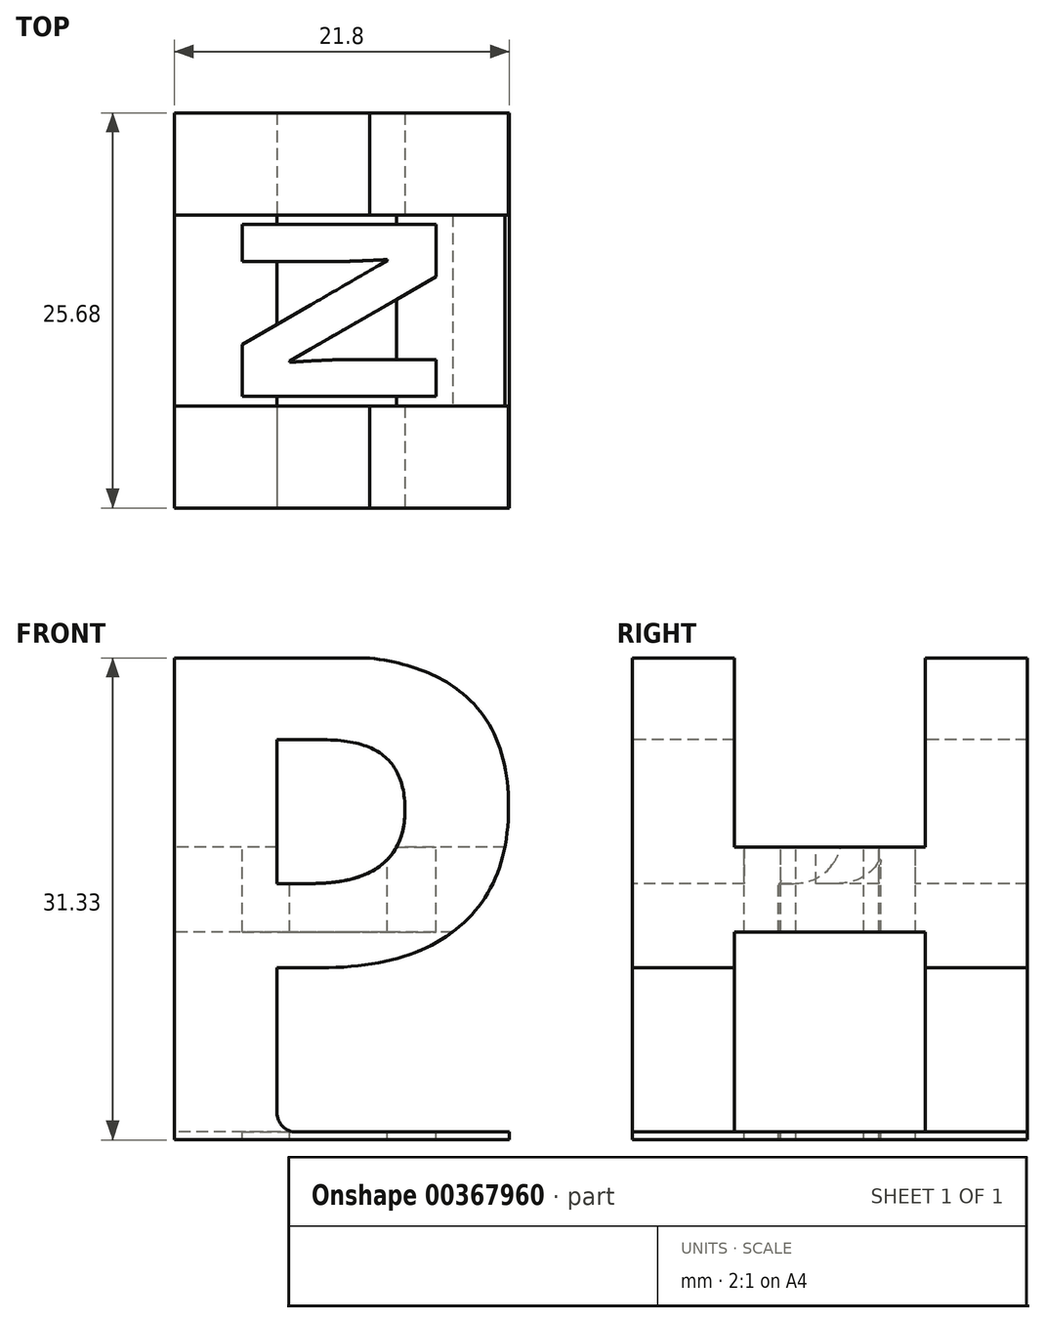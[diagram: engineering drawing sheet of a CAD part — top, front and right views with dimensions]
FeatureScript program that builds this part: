
annotation { "Feature Type Name" : "Feature", "Feature Type Description" : "" }
export const myFeature = defineFeature(function(context is Context, id is Id, definition is map)
    precondition{}
    {
        {
            var Q0;
            Q0=qCreatedBy(makeId("Front.planeOp"),FACE);
            var sketch = newSketch(context, id + "F0", { "sketchPlane" : qUnion([Q0])});
            skLineSegment(sketch, "E0.bottom", {"start": v(15.88, 15.88) * mm, "end": v(-15.88, 15.88) * mm});
            skLineSegment(sketch, "E0.top", {"start": v(15.88, -15.88) * mm, "end": v(-15.88, -15.88) * mm});
            skLineSegment(sketch, "E0.left", {"start": v(15.88, 15.88) * mm, "end": v(15.88, -15.88) * mm});
            skLineSegment(sketch, "E0.right", {"start": v(-15.88, 15.88) * mm, "end": v(-15.88, -15.88) * mm});
            skPoint(sketch, "E0.middle", {"position": v(0, 0) * mm});
            skSolve(sketch);
        }
        {
            var Q0;
            Q0=qSketchRegion(id+"F0",true);
            extrude(context, id + "F1", {"entities" : qUnion([Q0]), "depth" : 31.75 * mm});
        }
        {
            var Q0;
            Q0=makeQuery(id+"F1.opExtrude","CAP_FACE",FACE,{"disambiguationData":[OSD([sQuery(id+"F0.wireOp",EDGE,"E0.bottom"),sQuery(id+"F0.wireOp",EDGE,"E0.top"),sQuery(id+"F0.wireOp",EDGE,"E0.left"),sQuery(id+"F0.wireOp",EDGE,"E0.right")])],"isStart":false});
            var sketch = newSketch(context, id + "F2", { "sketchPlane" : qUnion([Q0])});
            skText(sketch, "E1", { "text": "P", "fontName": "OpenSans-Bold.ttf"});
            skLineSegment(sketch, "E2.bottom", {"start": v(11.48, -15.37) * mm, "end": v(-5.52, -15.37) * mm});
            skLineSegment(sketch, "E2.top", {"start": v(11.48, -15.88) * mm, "end": v(-5.52, -15.88) * mm});
            skLineSegment(sketch, "E2.left", {"start": v(11.48, -15.37) * mm, "end": v(11.48, -15.88) * mm});
            skLineSegment(sketch, "E2.right", {"start": v(-5.52, -15.37) * mm, "end": v(-5.52, -15.88) * mm});
            skLineSegment(sketch, "E3", {"start": v(11.48, 13.63) * mm, "end": v(11.48, -15.88) * mm, "construction": true});
            const initialGuessF2  = {"E1": [-0.01428, -0.01588, 1, 0, 0.03175]};
            skSetInitialGuess(sketch, initialGuessF2);
            skSolve(sketch);
        }
        {
            var Q0;
            Q0=makeQuery(id+"F2.imprint","IMPRINT",FACE,{"disambiguationData":[TD([[makeQuery(id+"F2.imprint","IMPRINT",EDGE,{"derivedFrom":sQuery(id+"F2.wireOp",EDGE,"E1.sketch_text.stroke-7")}),1.0]])]});
            var Q1;
            Q1=makeQuery(id+"F2.imprint","IMPRINT",FACE,{"disambiguationData":[TD([[makeQuery(id+"F2.imprint","IMPRINT",EDGE,{"derivedFrom":sQuery(id+"F2.wireOp",EDGE,"E1.sketch_text.stroke-0")}),1.0]])]});
            var Q2;
            {var subQ6=sQuery(id+"F2.wireOp",EDGE,"E1.sketch_text.stroke-9");Q2=makeQuery(id+"F2.imprint","IMPRINT",FACE,{"disambiguationData":[TD([[makeQuery(id+"F2.imprint","IMPRINT",EDGE,{"derivedFrom":subQ6}),1.0]])]});}
            var Q3;
            {var subQ1=sQuery(id+"F2.wireOp",EDGE,"86d704e9-ed5c-438c-a19e-a56261acf02c.sketch_text.stroke-1");Q3=makeQuery(id+"F2.imprint","IMPRINT",FACE,{"disambiguationData":[TD([[makeQuery(id+"F2.imprint","IMPRINT",EDGE,{"derivedFrom":subQ1}),1.0]])]});}
            var Q4;
            {var subQ0=sQuery(id+"F2.wireOp",EDGE,"3e470cdb-64af-4909-ac97-25825973aa04.sketch_text.stroke-1");Q4=makeQuery(id+"F2.imprint","IMPRINT",FACE,{"disambiguationData":[TD([[makeQuery(id+"F2.imprint","IMPRINT",EDGE,{"derivedFrom":subQ0}),1.0]])]});}
            var Q5;
            {var subQ1=makeQuery(id+"F1.opExtrude","CAP_EDGE",EDGE,{"disambiguationData":[OSD([sQuery(id+"F0.wireOp",EDGE,"E0.top")])],"isStart":false});var subQ3=makeQuery(id+"F1.opExtrude","CAP_EDGE",EDGE,{"disambiguationData":[OSD([sQuery(id+"F0.wireOp",EDGE,"E0.left")])],"isStart":false});var subQ5=makeQuery(id+"F2.imprint","INTERSECT",VERTEX,{"derivedFrom":[subQ1,subQ3]});Q5=makeQuery(id+"F2.imprint","IMPRINT",FACE,{"disambiguationData":[TD([[makeQuery(id+"F2.imprint","IMPRINT",EDGE,{"disambiguationData":[TD([[subQ5,1.0]])],"derivedFrom":subQ3}),-1.0]])]});}
            var Q6;
            {var subQ5=sQuery(id+"F2.wireOp",EDGE,"86d704e9-ed5c-438c-a19e-a56261acf02c.sketch_text.stroke-11");Q6=makeQuery(id+"F2.imprint","IMPRINT",FACE,{"disambiguationData":[TD([[makeQuery(id+"F2.imprint","IMPRINT",EDGE,{"derivedFrom":subQ5}),1.0]])]});}
            var Q7;
            {var subQ0=sQuery(id+"F2.wireOp",EDGE,"86d704e9-ed5c-438c-a19e-a56261acf02c.sketch_text.stroke-0");Q7=makeQuery(id+"F2.imprint","IMPRINT",FACE,{"disambiguationData":[TD([[makeQuery(id+"F2.imprint","IMPRINT",EDGE,{"derivedFrom":subQ0}),-1.0]])]});}
            extrude(context, id + "F3", {"entities" : qUnion([Q0, Q1, Q2, Q3, Q4, Q5, Q6, Q7]), "operationType" : NewBodyOperationType.REMOVE, "endBound" : BoundingType.THROUGH_ALL, "oppositeDirection" : true, "depth" : 25.4 * mm});
        }
        {
            var Q0;
            Q0=makeQuery(id+"F3.boolean.opBoolean","COPY",FACE,{"derivedFrom":makeQuery(id+"F3.opExtrude","SWEPT_FACE",FACE,{"disambiguationData":[OSD([sQuery(id+"F2.wireOp",EDGE,"E1.sketch_text.stroke-12")])]})});
            var sketch = newSketch(context, id + "F4", { "sketchPlane" : qUnion([Q0])});
            skText(sketch, "E4", { "text": "H", "fontName": "OpenSans-Bold.ttf"});
            skLineSegment(sketch, "E5.bottom", {"start": v(8.61, -15.88) * mm, "end": v(23.96, -15.88) * mm});
            skLineSegment(sketch, "E5.top", {"start": v(8.61, -15.37) * mm, "end": v(23.96, -15.37) * mm});
            skLineSegment(sketch, "E5.left", {"start": v(8.61, -15.88) * mm, "end": v(8.61, -15.37) * mm});
            skLineSegment(sketch, "E5.right", {"start": v(23.96, -15.88) * mm, "end": v(23.96, -15.37) * mm});
            const initialGuessF4  = {"E4": [-0.0011, -0.01588, 1, 0, 0.0316]};
            skSetInitialGuess(sketch, initialGuessF4);
            skSolve(sketch);
        }
        {
            var Q0;
            {var subQ5=sQuery(id+"F4.wireOp",EDGE,"E4.sketch_text.stroke-5");Q0=makeQuery(id+"F4.imprint","IMPRINT",FACE,{"disambiguationData":[TD([[makeQuery(id+"F4.imprint","IMPRINT",EDGE,{"derivedFrom":subQ5}),1.0]])]});}
            var Q1;
            {var subQ0=sQuery(id+"F4.wireOp",EDGE,"E4.sketch_text.stroke-2");Q1=makeQuery(id+"F4.imprint","IMPRINT",FACE,{"disambiguationData":[TD([[makeQuery(id+"F4.imprint","IMPRINT",EDGE,{"derivedFrom":subQ0}),1.0]])]});}
            extrude(context, id + "F5", {"entities" : qUnion([Q0, Q1]), "operationType" : NewBodyOperationType.REMOVE, "endBound" : BoundingType.THROUGH_ALL, "oppositeDirection" : true, "depth" : 25.4 * mm});
        }
        {
            var Q0;
            Q0=makeQuery(id+"F5.boolean.opBoolean","COPY",FACE,{"derivedFrom":makeQuery(id+"F5.opExtrude","SWEPT_FACE",FACE,{"disambiguationData":[OSD([sQuery(id+"F4.wireOp",EDGE,"E4.sketch_text.stroke-6")])]})});
            var sketch = newSketch(context, id + "F6", { "sketchPlane" : qUnion([Q0])});
            skText(sketch, "E6", { "text": "N", "fontName": "OpenSans-Bold.ttf"});
            const initialGuessF6  = {"E6": [0.0067, -0.02285, 0, 1, 0.0127]};
            skSetInitialGuess(sketch, initialGuessF6);
            skSolve(sketch);
        }
        {
            var Q0;
            Q0=makeQuery(id+"F6.imprint","IMPRINT",FACE,{"disambiguationData":[TD([[makeQuery(id+"F6.imprint","IMPRINT",EDGE,{"derivedFrom":sQuery(id+"F6.wireOp",EDGE,"E6.sketch_text.stroke-0")}),-1.0]])]});
            extrude(context, id + "F7", {"entities" : qUnion([Q0]), "operationType" : NewBodyOperationType.REMOVE, "endBound" : BoundingType.THROUGH_ALL, "oppositeDirection" : true, "depth" : 25.4 * mm});
        }
        {
            var Q0;
            {var subQ0=sQuery(id+"F2.wireOp",EDGE,"E2.bottom");var subQ1=sQuery(id+"F2.wireOp",EDGE,"E1.sketch_text.stroke-10");Q0=makeQuery(id+"F5.boolean.opBoolean","SPLIT",EDGE,{"disambiguationData":[TD([makeQuery(id+"F5.opExtrude","SWEPT_FACE",FACE,{"disambiguationData":[OSD([sQuery(id+"F4.wireOp",EDGE,"E4.sketch_text.stroke-1")])]})])],"derivedFrom":makeQuery(id+"F3.boolean.opBoolean","COPY",EDGE,{"derivedFrom":makeQuery(id+"F3.opExtrude","SWEPT_EDGE",EDGE,{"disambiguationData":[OSD([subQ1,subQ0])]})})});}
            var Q1;
            {var subQ0=sQuery(id+"F2.wireOp",EDGE,"E2.bottom");var subQ1=sQuery(id+"F2.wireOp",EDGE,"E1.sketch_text.stroke-10");Q1=makeQuery(id+"F5.boolean.opBoolean","SPLIT",EDGE,{"disambiguationData":[TD([makeQuery(id+"F5.opExtrude","SWEPT_FACE",FACE,{"disambiguationData":[OSD([sQuery(id+"F4.wireOp",EDGE,"E4.sketch_text.stroke-3")])]})])],"derivedFrom":makeQuery(id+"F3.boolean.opBoolean","COPY",EDGE,{"derivedFrom":makeQuery(id+"F3.opExtrude","SWEPT_EDGE",EDGE,{"disambiguationData":[OSD([subQ1,subQ0])]})})});}
            fillet(context, id + "F8", {"entities" : qUnion([Q0, Q1]), "tangentPropagation" : true, "radius" : 1.27 * mm, "defaultsChanged" : true, "vertexSettings" : [], "allowEdgeOverflow" : false});
        }
    });
